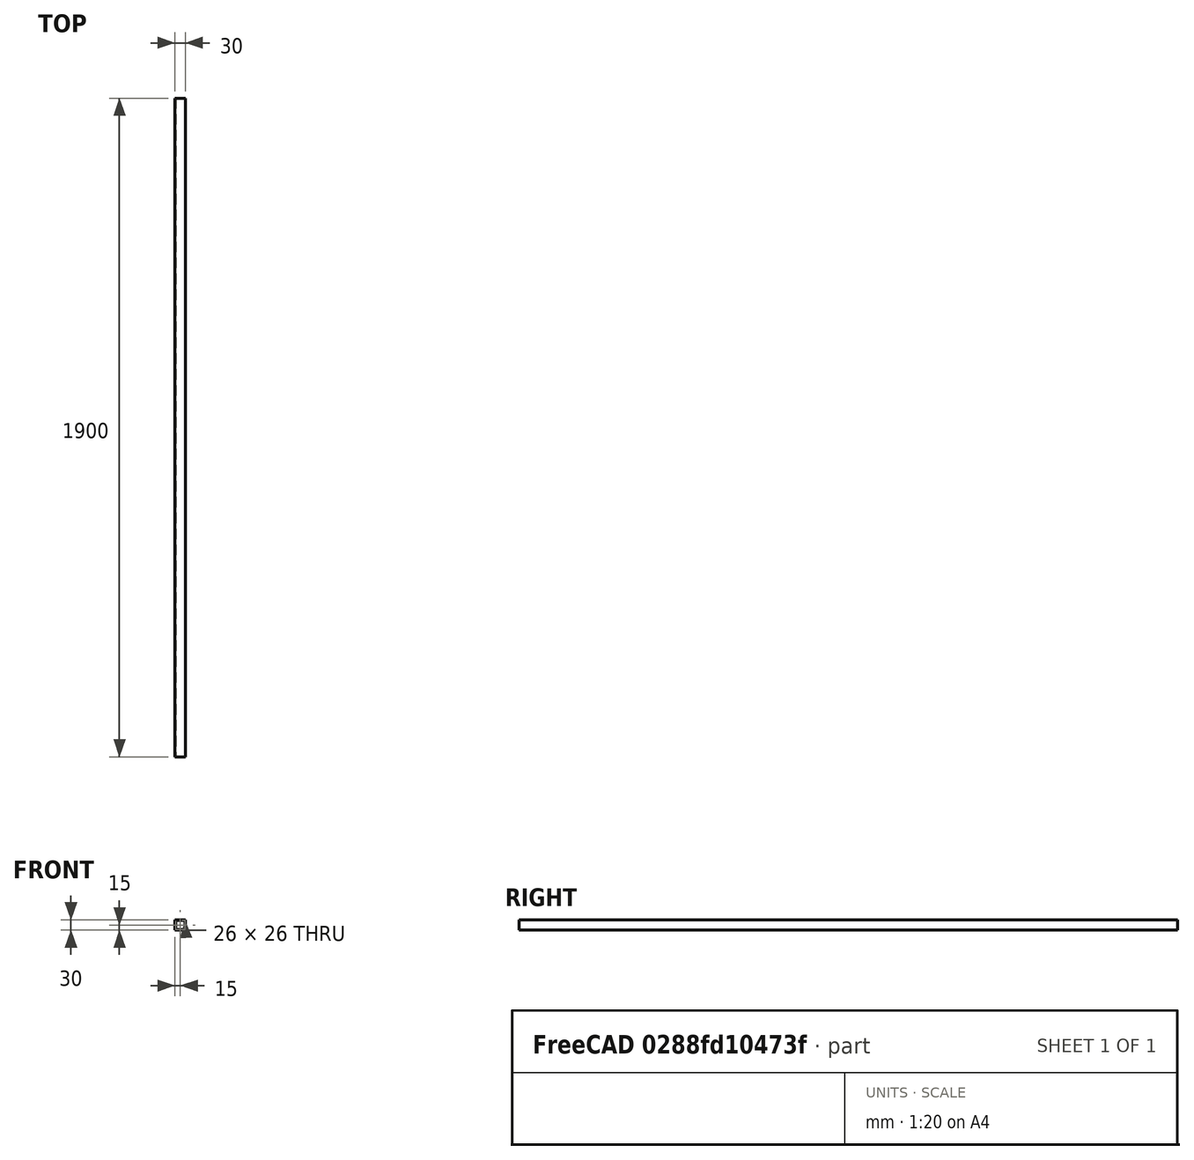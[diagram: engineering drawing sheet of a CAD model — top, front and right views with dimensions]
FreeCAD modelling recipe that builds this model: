
FCSTD DOCUMENT  (FreeCAD 0.20R29177 +426 (Git))
Label: beam_long_bottom
License: All rights reserved
LicenseURL: http://en.wikipedia.org/wiki/All_rights_reserved
objects: Sketcher::SketchObject×1, PartDesign::Pad×1, PartDesign::Body×1
note: 4 computed .brp shape members not serialized (recipe doc carries the construction recipe); baked Part::Feature solids carry a one-line shape summary decoded from their .brp

FEATURE [Sketcher::SketchObject] Sketch
  FullyConstrained = true
  MapMode = 5
  Placement = pos=(0,0,0) rot=(1,0,0;1.5708rad)
  Support = -> [XZ_Plane]
  sketch-geometry (10):
    g0: LineSegment StartX=0 StartY=0 StartZ=0 EndX=30 EndY=0 EndZ=0
    g1: LineSegment StartX=30 StartY=0 StartZ=0 EndX=30 EndY=30 EndZ=0
    g2: LineSegment StartX=30 StartY=30 StartZ=0 EndX=0 EndY=30 EndZ=0
    g3: LineSegment StartX=0 StartY=30 StartZ=0 EndX=0 EndY=0 EndZ=0
    g4: LineSegment StartX=2 StartY=28 StartZ=0 EndX=28 EndY=28 EndZ=0
    g5: LineSegment StartX=28 StartY=28 StartZ=0 EndX=28 EndY=2 EndZ=0
    g6: LineSegment StartX=28 StartY=2 StartZ=0 EndX=2 EndY=2 EndZ=0
    g7: LineSegment StartX=2 StartY=2 StartZ=0 EndX=2 EndY=28 EndZ=0
    g8: LineSegment StartX=0 StartY=0 StartZ=0 EndX=30 EndY=30 EndZ=0
    g9: LineSegment StartX=0 StartY=30 StartZ=0 EndX=30 EndY=0 EndZ=0
  constraints (27):
    c: Coincident(g0,g1)
    c: Coincident(g1,g2)
    c: Coincident(g2,g3)
    c: Coincident(g3,g0)
    c: Horizontal(g0)
    c: Horizontal(g2)
    c: Vertical(g1)
    c: Vertical(g3)
    c: Coincident(g0,g-1)
    c: DistanceX(g2,g2) = 30
    c: Coincident(g4,g5)
    c: Coincident(g5,g6)
    c: Coincident(g6,g7)
    c: Coincident(g7,g4)
    c: Horizontal(g4)
    c: Horizontal(g6)
    c: Vertical(g5)
    c: Vertical(g7)
    c: DistanceY(g4,g1) = 2
    c: Equal(g1,g2)
    c: Equal(g4,g5)
    c: Coincident(g8,g0)
    c: Coincident(g8,g1)
    c: PointOnObject(g4,g8)
    c: Coincident(g9,g2)
    c: Coincident(g9,g0)
    c: PointOnObject(g4,g9)
FEATURE [PartDesign::Pad] Pad
  Direction = (0,-1,-2e-16)
  Length = 1900
  Length2 = 10
  Placement = pos=(0,0,0) rot=(1,0,0;1.5708rad)
  Profile = -> Sketch
  ReferenceAxis = -> Sketch [N_Axis]
  Refine = true
  Type = 0
FEATURE [PartDesign::Body] Body
  Group = -> [Sketch,Pad]
  Origin = -> Origin
  Tip = -> Pad
